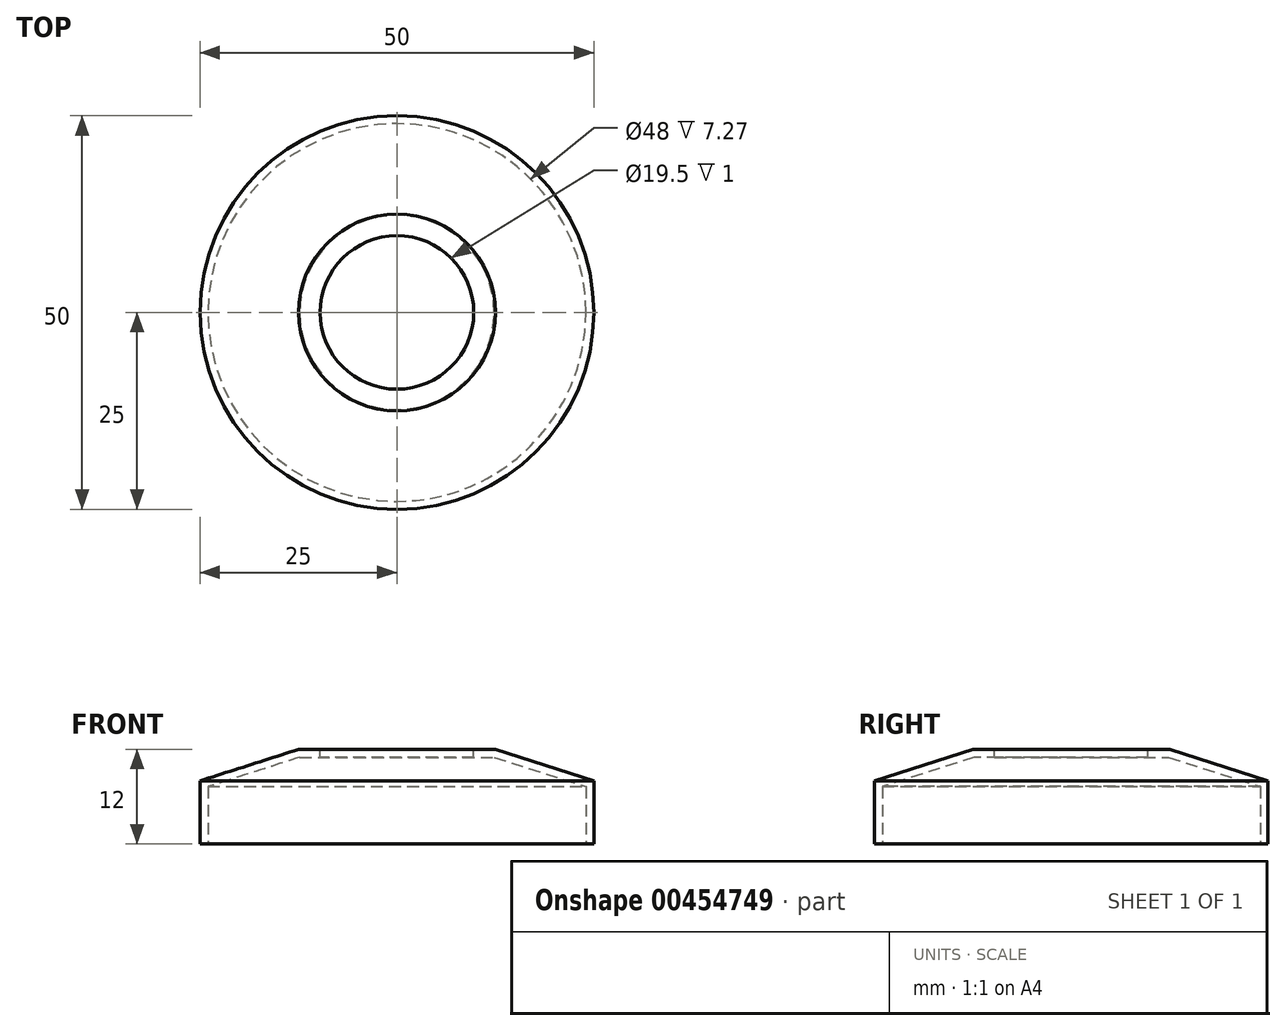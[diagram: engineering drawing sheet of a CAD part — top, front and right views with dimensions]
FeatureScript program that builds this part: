
annotation { "Feature Type Name" : "Feature", "Feature Type Description" : "" }
export const myFeature = defineFeature(function(context is Context, id is Id, definition is map)
    precondition{}
    {
        {
            var Q0;
            Q0=qCreatedBy(makeId("Front.planeOp"),FACE);
            var sketch = newSketch(context, id + "F0", { "sketchPlane" : qUnion([Q0])});
            skLineSegment(sketch, "E0", {"start": v(0, 0) * mm, "end": v(0, 78.35) * mm, "construction": true});
            skLineSegment(sketch, "E1", {"start": v(0, 0) * mm, "end": v(25, 0) * mm});
            skLineSegment(sketch, "E2", {"start": v(25, 0) * mm, "end": v(25, 8) * mm});
            skLineSegment(sketch, "E3", {"start": v(25, 8) * mm, "end": v(12.5, 12) * mm});
            skLineSegment(sketch, "E4", {"start": v(12.5, 12) * mm, "end": v(0, 12) * mm});
            skLineSegment(sketch, "E5", {"start": v(0, 12) * mm, "end": v(0, 0) * mm});
            skSolve(sketch);
        }
        {
            var Q0;
            Q0=makeQuery(id+"F0.imprint","IMPRINT",FACE,{"disambiguationData":[TD([[makeQuery(id+"F0.imprint","IMPRINT",EDGE,{"derivedFrom":sQuery(id+"F0.wireOp",EDGE,"E1")}),1.0]])]});
            var Q1;
            Q1=sQuery(id+"F0.wireOp",EDGE,"E0");
            revolve(context, id + "F1", {"entities" : qUnion([Q0]), "axis" : qUnion([Q1]), "revolveType" : RevolveType.FULL});
        }
        {
            var Q0;
            Q0=makeQuery(id+"F1.opRevolve","SWEPT_FACE",FACE,{"disambiguationData":[OSD([sQuery(id+"F0.wireOp",EDGE,"E1")])]});
            shell(context, id + "F2", {"entities" : qUnion([Q0]), "thickness" : 1 * mm});
        }
        {
            var Q0;
            Q0=makeQuery(id+"F1.opRevolve","SWEPT_FACE",FACE,{"disambiguationData":[OSD([sQuery(id+"F0.wireOp",EDGE,"E4")])]});
            var sketch = newSketch(context, id + "F3", { "sketchPlane" : qUnion([Q0])});
            skCircle(sketch, "E6", {"center": v(0, 0) * mm, "radius": 9.75 * mm});
            skSolve(sketch);
        }
        {
            var Q0;
            Q0 = qSketchRegion(id + "F3", true);
            extrude(context, id + "F4", {"entities" : qUnion([Q0]), "operationType" : NewBodyOperationType.REMOVE, "endBound" : BoundingType.UP_TO_NEXT, "oppositeDirection" : true, "depth" : 25 * mm});
        }
    });
